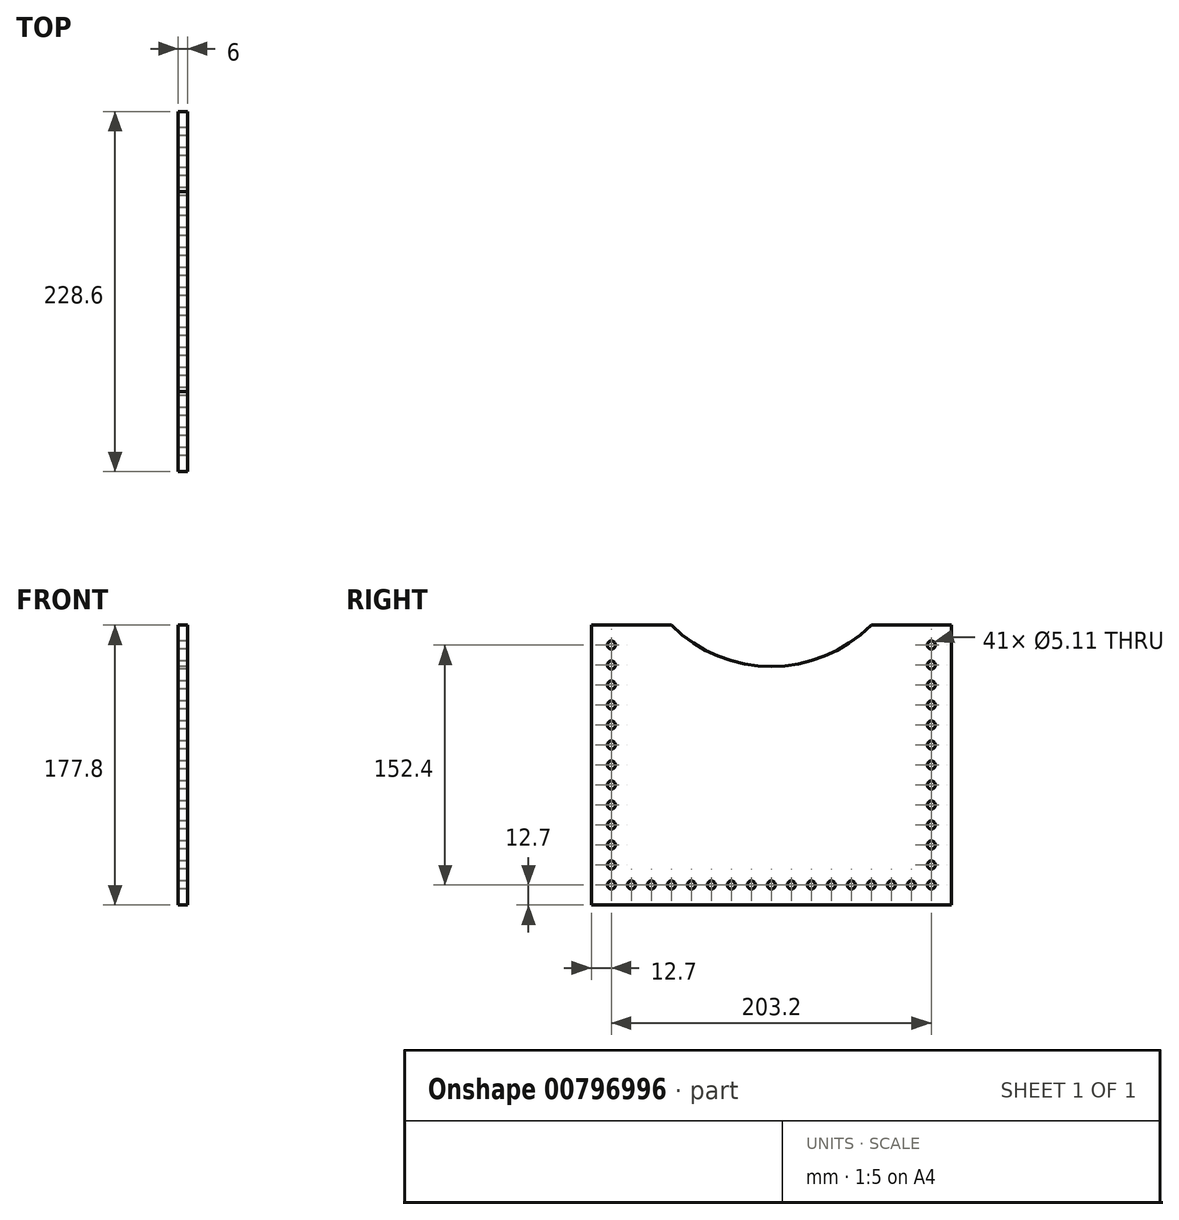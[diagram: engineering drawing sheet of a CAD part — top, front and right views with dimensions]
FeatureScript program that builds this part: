
annotation { "Feature Type Name" : "Feature", "Feature Type Description" : "" }
export const myFeature = defineFeature(function(context is Context, id is Id, definition is map)
    precondition{}
    {
        {
            var Q0;
            Q0=qCreatedBy(makeId("Right.planeOp"),FACE);
            var sketch = newSketch(context, id + "F0", { "sketchPlane" : qUnion([Q0])});
            skLineSegment(sketch, "E0.bottom", {"start": v(-114.3, 0) * mm, "end": v(114.3, 0) * mm, "construction": true});
            skLineSegment(sketch, "E0.top", {"start": v(-114.3, 177.8) * mm, "end": v(114.3, 177.8) * mm, "construction": true});
            skLineSegment(sketch, "E0.left", {"start": v(-114.3, 0) * mm, "end": v(-114.3, 177.8) * mm, "construction": true});
            skLineSegment(sketch, "E0.right", {"start": v(114.3, 0) * mm, "end": v(114.3, 177.8) * mm, "construction": true});
            skPoint(sketch, "E0.middle", {"position": v(0, 88.9) * mm});
            skLineSegment(sketch, "E1", {"start": v(-114.3, 177.8) * mm, "end": v(-114.3, 0) * mm});
            skLineSegment(sketch, "E2", {"start": v(-114.3, 0) * mm, "end": v(114.3, 0) * mm});
            skLineSegment(sketch, "E3", {"start": v(114.3, 0) * mm, "end": v(114.3, 177.8) * mm});
            skLineSegment(sketch, "E4", {"start": v(114.3, 177.8) * mm, "end": v(63.5, 177.8) * mm});
            skLineSegment(sketch, "E5", {"start": v(-114.3, 177.8) * mm, "end": v(-63.5, 177.8) * mm});
            skArc(sketch, "E6", {"start": v(-63.5, 177.8) * mm, "mid": v(0, 151.5) * mm, "end": v(63.5, 177.8) * mm});
            skCircle(sketch, "E7", {"center": v(-101.6, 165.1) * mm, "radius": 2.55 * mm});
            skCircle(sketch, "E8.1.0.0", {"center": v(-88.9, 165.1) * mm, "radius": 2.55 * mm, "construction": true});
            skCircle(sketch, "E8.2.0.0", {"center": v(-76.2, 165.1) * mm, "radius": 2.55 * mm, "construction": true});
            skCircle(sketch, "E8.15.0.0", {"center": v(88.9, 165.1) * mm, "radius": 2.55 * mm, "construction": true});
            skCircle(sketch, "E8.16.0.0", {"center": v(101.6, 165.1) * mm, "radius": 2.55 * mm});
            skLineSegment(sketch, "E8.direction1", {"start": v(-101.6, 165.1) * mm, "end": v(-88.9, 165.1) * mm, "construction": true});
            skCircle(sketch, "E9.0.1.0", {"center": v(-101.6, 152.4) * mm, "radius": 2.55 * mm});
            skCircle(sketch, "E9.0.2.0", {"center": v(-101.6, 139.7) * mm, "radius": 2.55 * mm});
            skCircle(sketch, "E9.0.3.0", {"center": v(-101.6, 127) * mm, "radius": 2.55 * mm});
            skCircle(sketch, "E9.0.4.0", {"center": v(-101.6, 114.3) * mm, "radius": 2.55 * mm});
            skCircle(sketch, "E9.0.5.0", {"center": v(-101.6, 101.6) * mm, "radius": 2.55 * mm});
            skCircle(sketch, "E9.0.6.0", {"center": v(-101.6, 88.9) * mm, "radius": 2.55 * mm});
            skCircle(sketch, "E9.0.7.0", {"center": v(-101.6, 76.2) * mm, "radius": 2.55 * mm});
            skCircle(sketch, "E9.0.8.0", {"center": v(-101.6, 63.5) * mm, "radius": 2.55 * mm});
            skCircle(sketch, "E9.0.9.0", {"center": v(-101.6, 50.8) * mm, "radius": 2.55 * mm});
            skCircle(sketch, "E9.0.10.0", {"center": v(-101.6, 38.1) * mm, "radius": 2.55 * mm});
            skCircle(sketch, "E9.0.11.0", {"center": v(-101.6, 25.4) * mm, "radius": 2.55 * mm});
            skCircle(sketch, "E9.0.12.0", {"center": v(-101.6, 12.7) * mm, "radius": 2.55 * mm});
            skLineSegment(sketch, "E9.direction1", {"start": v(-101.6, 165.1) * mm, "end": v(-101.6, 165.1) * mm});
            skLineSegment(sketch, "E9.direction2", {"start": v(-101.6, 165.1) * mm, "end": v(-101.6, 152.4) * mm, "construction": true});
            skCircle(sketch, "E10.1.0.0", {"center": v(-88.9, 12.7) * mm, "radius": 2.55 * mm});
            skCircle(sketch, "E10.2.0.0", {"center": v(-76.2, 12.7) * mm, "radius": 2.55 * mm});
            skCircle(sketch, "E10.3.0.0", {"center": v(-63.5, 12.7) * mm, "radius": 2.55 * mm});
            skCircle(sketch, "E10.4.0.0", {"center": v(-50.8, 12.7) * mm, "radius": 2.55 * mm});
            skCircle(sketch, "E10.5.0.0", {"center": v(-38.1, 12.7) * mm, "radius": 2.55 * mm});
            skCircle(sketch, "E10.6.0.0", {"center": v(-25.4, 12.7) * mm, "radius": 2.55 * mm});
            skCircle(sketch, "E10.7.0.0", {"center": v(-12.7, 12.7) * mm, "radius": 2.55 * mm});
            skCircle(sketch, "E10.8.0.0", {"center": v(0, 12.7) * mm, "radius": 2.55 * mm});
            skCircle(sketch, "E10.9.0.0", {"center": v(12.7, 12.7) * mm, "radius": 2.55 * mm});
            skCircle(sketch, "E10.10.0.0", {"center": v(25.4, 12.7) * mm, "radius": 2.55 * mm});
            skCircle(sketch, "E10.11.0.0", {"center": v(38.1, 12.7) * mm, "radius": 2.55 * mm});
            skCircle(sketch, "E10.12.0.0", {"center": v(50.8, 12.7) * mm, "radius": 2.55 * mm});
            skCircle(sketch, "E10.13.0.0", {"center": v(63.5, 12.7) * mm, "radius": 2.55 * mm});
            skCircle(sketch, "E10.14.0.0", {"center": v(76.2, 12.7) * mm, "radius": 2.55 * mm});
            skCircle(sketch, "E10.15.0.0", {"center": v(88.9, 12.7) * mm, "radius": 2.55 * mm});
            skCircle(sketch, "E10.16.0.0", {"center": v(101.6, 12.7) * mm, "radius": 2.55 * mm});
            skLineSegment(sketch, "E10.direction1", {"start": v(-101.6, 12.7) * mm, "end": v(-88.9, 12.7) * mm, "construction": true});
            skCircle(sketch, "E11.0.1.0", {"center": v(101.6, 152.4) * mm, "radius": 2.55 * mm});
            skCircle(sketch, "E11.0.2.0", {"center": v(101.6, 139.7) * mm, "radius": 2.55 * mm});
            skCircle(sketch, "E11.0.3.0", {"center": v(101.6, 127) * mm, "radius": 2.55 * mm});
            skCircle(sketch, "E11.0.4.0", {"center": v(101.6, 114.3) * mm, "radius": 2.55 * mm});
            skCircle(sketch, "E11.0.5.0", {"center": v(101.6, 101.6) * mm, "radius": 2.55 * mm});
            skCircle(sketch, "E11.0.6.0", {"center": v(101.6, 88.9) * mm, "radius": 2.55 * mm});
            skCircle(sketch, "E11.0.7.0", {"center": v(101.6, 76.2) * mm, "radius": 2.55 * mm});
            skCircle(sketch, "E11.0.8.0", {"center": v(101.6, 63.5) * mm, "radius": 2.55 * mm});
            skCircle(sketch, "E11.0.9.0", {"center": v(101.6, 50.8) * mm, "radius": 2.55 * mm});
            skCircle(sketch, "E11.0.10.0", {"center": v(101.6, 38.1) * mm, "radius": 2.55 * mm});
            skCircle(sketch, "E11.0.11.0", {"center": v(101.6, 25.4) * mm, "radius": 2.55 * mm});
            skLineSegment(sketch, "E11.direction1", {"start": v(101.6, 165.1) * mm, "end": v(127, 165.1) * mm, "construction": true});
            skLineSegment(sketch, "E11.direction2", {"start": v(101.6, 165.1) * mm, "end": v(101.6, 152.4) * mm, "construction": true});
            skLineSegment(sketch, "E12", {"start": v(0, 12.7) * mm, "end": v(0, 0) * mm, "construction": true});
            skSolve(sketch);
        }
        {
            var Q0;
            Q0 = qSketchRegion(id + "F0", true);
            extrude(context, id + "F1", {"entities" : qUnion([Q0]), "depth" : 6 * mm, "offsetDistance" : 25.4 * mm});
        }
    });
